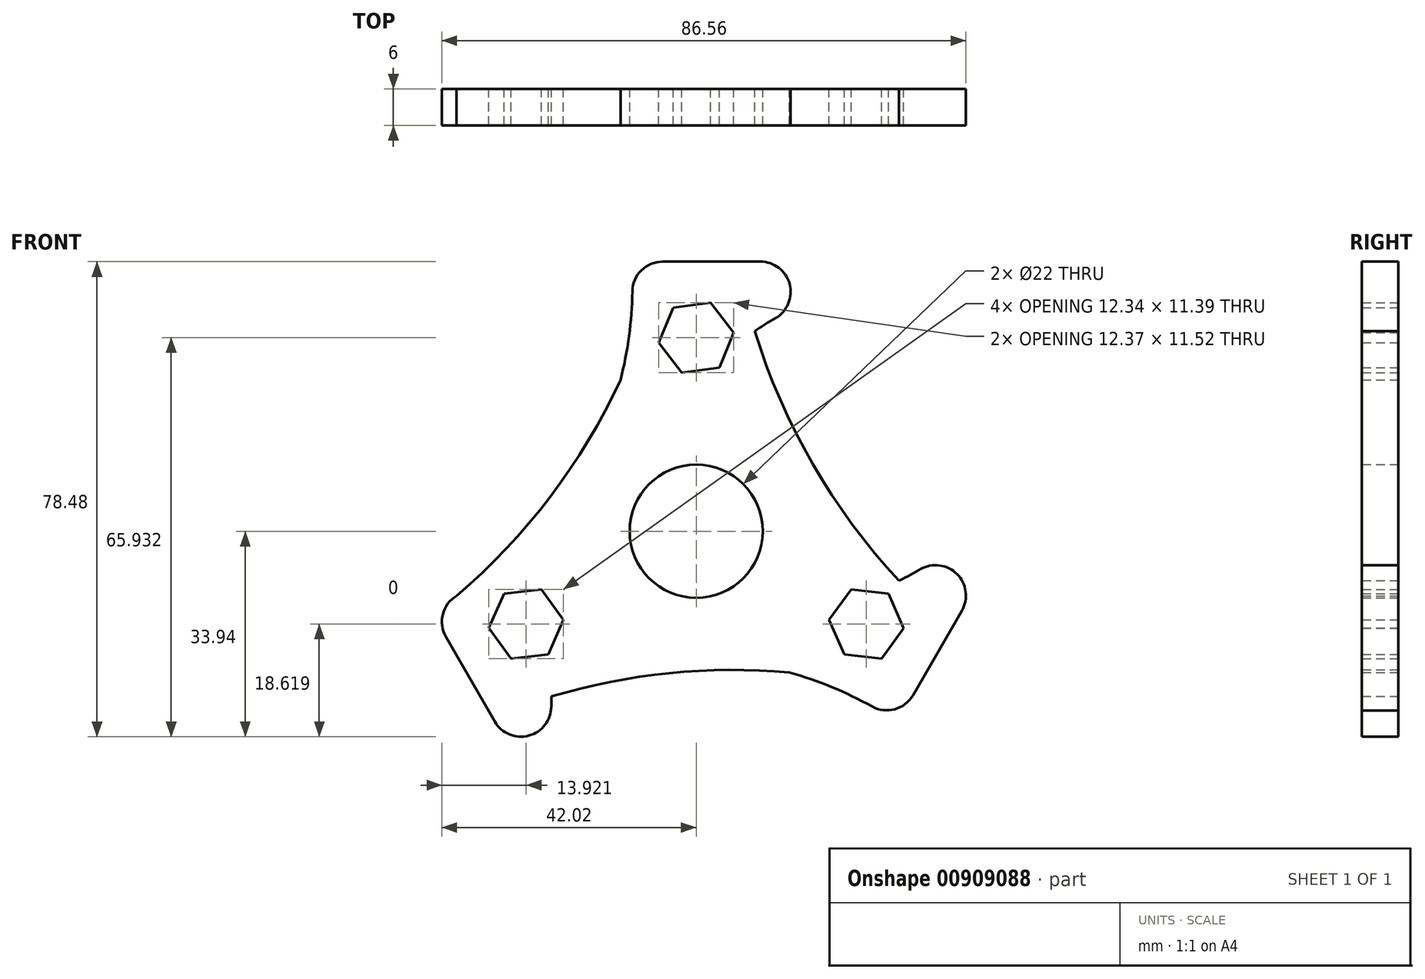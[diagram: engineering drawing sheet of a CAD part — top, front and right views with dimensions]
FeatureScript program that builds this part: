
annotation { "Feature Type Name" : "Feature", "Feature Type Description" : "" }
export const myFeature = defineFeature(function(context is Context, id is Id, definition is map)
    precondition{}
    {
        {
            var Q0;
            Q0=qCreatedBy(makeId("Front.planeOp"),FACE);
            var sketch = newSketch(context, id + "F0", { "sketchPlane" : qUnion([Q0])});
            skLineSegment(sketch, "E0", {"start": v(10.59, 44.54) * mm, "end": v(-5.56, 44.54) * mm});
            skPoint(sketch, "E1.MirrorCS.end.orphan", {"position": v(-10.69, 44.54) * mm});
            skPoint(sketch, "E2.MirrorCS.end.orphan", {"position": v(10.93, 44.54) * mm});
            skPoint(sketch, "E3.MirrorP", {"position": v(44.04, -12.8) * mm});
            skPoint(sketch, "E4.MirrorP", {"position": v(-42.29, -13.46) * mm});
            skPoint(sketch, "E5.MirrorP", {"position": v(-33.11, -31.73) * mm});
            skCircle(sketch, "E6.cCircle", {"center": v(0, 32) * mm, "radius": 6.24 * mm, "construction": true});
            skLineSegment(sketch, "E6.0", {"start": v(3.8, 27.04) * mm, "end": v(-2.39, 26.23) * mm});
            skLineSegment(sketch, "E6.1", {"start": v(-2.39, 26.23) * mm, "end": v(-6.18, 31.18) * mm});
            skLineSegment(sketch, "E6.2", {"start": v(-6.18, 31.18) * mm, "end": v(-3.8, 36.94) * mm});
            skLineSegment(sketch, "E6.3", {"start": v(-3.8, 36.94) * mm, "end": v(2.39, 37.75) * mm});
            skLineSegment(sketch, "E6.4", {"start": v(2.39, 37.75) * mm, "end": v(6.18, 32.8) * mm});
            skLineSegment(sketch, "E6.5", {"start": v(6.18, 32.8) * mm, "end": v(3.8, 27.04) * mm});
            skLineSegment(sketch, "E7.MirrorCS", {"start": v(25.58, -9.63) * mm, "end": v(21.93, -14.64) * mm});
            skLineSegment(sketch, "E8.MirrorCS", {"start": v(31.75, -10.28) * mm, "end": v(25.58, -9.63) * mm});
            skLineSegment(sketch, "E9.MirrorCS", {"start": v(21.93, -14.64) * mm, "end": v(24.44, -20.37) * mm});
            skCircle(sketch, "E10.MirrorC", {"center": v(27.7, -16) * mm, "radius": 6.2 * mm, "construction": true});
            skLineSegment(sketch, "E11.MirrorCS", {"start": v(30.62, -21.02) * mm, "end": v(34.27, -16) * mm});
            skLineSegment(sketch, "E12.MirrorCS", {"start": v(34.27, -16) * mm, "end": v(31.75, -10.28) * mm});
            skLineSegment(sketch, "E13.MirrorCS", {"start": v(24.44, -20.37) * mm, "end": v(30.62, -21.02) * mm});
            skLineSegment(sketch, "E14.MirrorCS", {"start": v(-34.27, -15.95) * mm, "end": v(-31.75, -10.28) * mm});
            skLineSegment(sketch, "E15.MirrorCS", {"start": v(-31.75, -10.28) * mm, "end": v(-25.58, -9.63) * mm});
            skLineSegment(sketch, "E16.MirrorCS", {"start": v(-30.62, -21.02) * mm, "end": v(-34.27, -15.95) * mm});
            skLineSegment(sketch, "E17.MirrorCS", {"start": v(-21.93, -14.64) * mm, "end": v(-24.44, -20.37) * mm});
            skLineSegment(sketch, "E18.MirrorCS", {"start": v(-25.58, -9.63) * mm, "end": v(-21.93, -14.64) * mm});
            skLineSegment(sketch, "E19.MirrorCS", {"start": v(-24.44, -20.37) * mm, "end": v(-30.62, -21.02) * mm});
            skCircle(sketch, "E20.MirrorC", {"center": v(-27.7, -16) * mm, "radius": 6.2 * mm, "construction": true});
            skLineSegment(sketch, "E21", {"start": v(-22.33, -12.9) * mm, "end": v(-22.94, -13.25) * mm});
            skLineSegment(sketch, "E22", {"start": v(22.33, -12.9) * mm, "end": v(22.94, -13.25) * mm});
            skArc(sketch, "E23", {"start": v(-12.53, 24.97) * mm, "mid": v(-11.1, 32.23) * mm, "end": v(-10.56, 39.6) * mm});
            skArc(sketch, "E24.MirrorCS", {"start": v(9.66, 33.07) * mm, "mid": v(11.36, 34.17) * mm, "end": v(13.1, 35.22) * mm});
            skArc(sketch, "E25.MirrorCS", {"start": v(33.47, -8.17) * mm, "mid": v(35.27, -7.25) * mm, "end": v(37.04, -6.27) * mm});
            skLineSegment(sketch, "E26.MirrorCS", {"start": v(43.87, -13.1) * mm, "end": v(35.8, -27.08) * mm});
            skArc(sketch, "E27.MirrorCS", {"start": v(15.36, -23.33) * mm, "mid": v(22.36, -25.73) * mm, "end": v(29.02, -28.95) * mm});
            skArc(sketch, "E28.MirrorCS", {"start": v(-23.81, -24.9) * mm, "mid": v(-23.92, -26.92) * mm, "end": v(-23.95, -28.95) * mm});
            skLineSegment(sketch, "E29.MirrorCS", {"start": v(-33.28, -31.44) * mm, "end": v(-41.35, -17.46) * mm});
            skArc(sketch, "E30", {"start": v(9.66, 33.07) * mm, "mid": v(19.25, 11.11) * mm, "end": v(33.47, -8.17) * mm});
            skArc(sketch, "E31.MirrorCS", {"start": v(-12.53, 24.97) * mm, "mid": v(-24.12, 5.7) * mm, "end": v(-39.58, -10.66) * mm});
            skArc(sketch, "E32.MirrorCS", {"start": v(15.36, -23.33) * mm, "mid": v(-7.13, -23.74) * mm, "end": v(-29.02, -28.95) * mm});
            skLineSegment(sketch, "E33.trimOffspring", {"start": v(0, 25.76) * mm, "end": v(0, 26.55) * mm});
            skCircle(sketch, "E34", {"center": v(0, 0) * mm, "radius": 11 * mm});
            skPoint(sketch, "E35.newPointA", {"position": v(15.06, 36.3) * mm});
            skArc(sketch, "E35.filletArc", {"start": v(13.1, 35.22) * mm, "mid": v(15.41, 40.84) * mm, "end": v(10.59, 44.54) * mm});
            skArc(sketch, "E36.filletArc", {"start": v(-5.56, 44.54) * mm, "mid": v(-9.07, 43.1) * mm, "end": v(-10.56, 39.6) * mm});
            skPoint(sketch, "E37.newPointA", {"position": v(38.98, -5.11) * mm});
            skArc(sketch, "E37.filletArc", {"start": v(43.87, -13.1) * mm, "mid": v(43.07, -7.07) * mm, "end": v(37.04, -6.27) * mm});
            skPoint(sketch, "E38.visualSharp", {"position": v(33.23, -31.53) * mm});
            skArc(sketch, "E38.filletArc", {"start": v(29.02, -28.95) * mm, "mid": v(32.8, -29.4) * mm, "end": v(35.8, -27.08) * mm});
            skPoint(sketch, "E39.newPointA", {"position": v(-23.91, -31.2) * mm});
            skArc(sketch, "E39.filletArc", {"start": v(-33.28, -31.44) * mm, "mid": v(-27.66, -33.77) * mm, "end": v(-23.95, -28.95) * mm});
            skPoint(sketch, "E40.visualSharp", {"position": v(-43.92, -13.01) * mm});
            skArc(sketch, "E40.filletArc", {"start": v(-39.58, -10.66) * mm, "mid": v(-41.86, -13.7) * mm, "end": v(-41.35, -17.46) * mm});
            skSolve(sketch);
        }
        {
            var Q0;
            Q0=makeQuery(id+"F0.imprint","IMPRINT",FACE,{"disambiguationData":[TD([[makeQuery(id+"F0.imprint","IMPRINT",EDGE,{"derivedFrom":sQuery(id+"F0.wireOp",EDGE,"E0")}),1.0]])]});
            extrude(context, id + "F1", {"entities" : qUnion([Q0]), "endBound" : BoundingType.SYMMETRIC, "depth" : 6 * mm, "offsetDistance" : 25 * mm});
        }
    });
